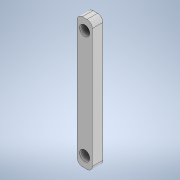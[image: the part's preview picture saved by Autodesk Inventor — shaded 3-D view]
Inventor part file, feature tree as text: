
AUTODESK INVENTOR PART (.ipt)
format: ipt  version: 2022 (Build 260153000, 153)  size: 116,736 bytes
history: native  units: in
note: dims shown in document units (in); Inventor stores cm internally (conversion verified against a paired STEP export)
features: extrude x1, fillet x1, sketch x1
ambient origin geometry x8: Origin, YZ Plane, XZ Plane, XY Plane, X Axis, Y Axis, Z Axis, Center Point
bodies: Solid1 (feature_tree)
feature tree (3):
  extrude  "Extrusion1"  Depth=0.0625in
  fillet  "Fillet2"  Radius=0.083in
  sketch  "Sketch1"  dims[d0=0.18in d1=1.45in d2=0.083in d3=0.12in d4=0.125in d5=0.0in d7=0.045in d8=0.0625in]
